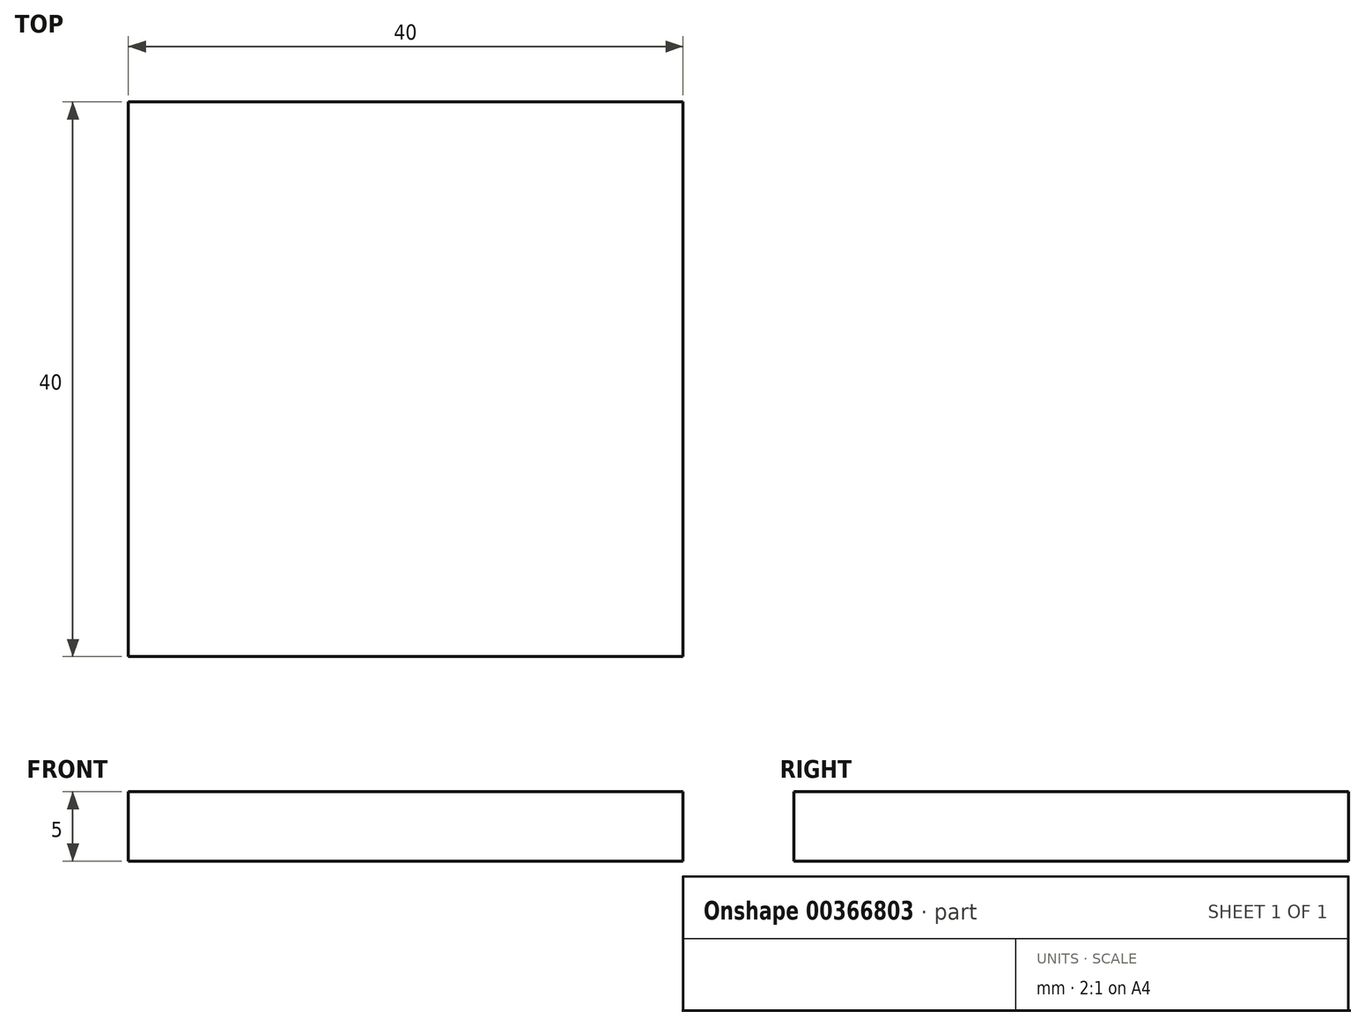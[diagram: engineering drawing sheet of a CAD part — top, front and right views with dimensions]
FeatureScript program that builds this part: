
annotation { "Feature Type Name" : "Feature", "Feature Type Description" : "" }
export const myFeature = defineFeature(function(context is Context, id is Id, definition is map)
    precondition{}
    {
        {
            var Q0;
            Q0=qCreatedBy(makeId("Top.planeOp"),FACE);
            var sketch = newSketch(context, id + "F0", { "sketchPlane" : qUnion([Q0])});
            skLineSegment(sketch, "E0.bottom", {"start": v(0, 0) * mm, "end": v(40, 0) * mm});
            skLineSegment(sketch, "E0.top", {"start": v(0, -40) * mm, "end": v(40, -40) * mm});
            skLineSegment(sketch, "E0.left", {"start": v(0, 0) * mm, "end": v(0, -40) * mm});
            skLineSegment(sketch, "E0.right", {"start": v(40, 0) * mm, "end": v(40, -40) * mm});
            skSolve(sketch);
        }
        {
            var Q0;
            Q0 = qConstructionFilter(qBodyType(qCreatedBy(id + "F0" ,EDGE), BodyType.WIRE), ConstructionObject.NO);
            var Q1;
            Q1 = qConstructionFilter(qBodyType(qCreatedBy(id + "F2" ,EDGE), BodyType.WIRE), ConstructionObject.NO);
            extrude(context, id + "F1", {"bodyType" : ToolBodyType.SURFACE, "surfaceEntities" : qUnion([Q0, Q1]), "depth" : 5 * mm});
        }
    });
